# Revit family: Legrand_Electric_vehicules_charging_stations_Green_up_Metal_Connected_charging_stations
name_source: partatom
category: Equipement électrique
units: mm (PartAtom-declared; Revit-internal decimal feet)

## family parameters
Basée sur le plan de construction = Non
Configuration du panneau = Deux colonnes, circuits au sein
Cote de connecteur circulaire = Utiliser le diamètre
Couper avec des vides une fois chargée = Non
Numéro OmniClass = 23.80.30.11.17
Partagée = Non
Point de calcul de pièce = Non
Titre OmniClass = Distribution Boards and Control Panels
Toujours verticalement = Oui
Type d'élément = Tableau de raccordement

## types (20) — shared parameters
ETIM Class 6.0 = EC002883
Fabricant = Legrand
IK = 08
IP = 44
Modèle = Green'up Legrand Metal Terminal
Tension = 220
URL = www.legrand.fr
trigger safety signal transmission = 406276
zero-valued in all types: Elévation par défaut

## per-type parameters (varying)
| type | Description | General Conditions of Use | Image du type | Puissance | adjustment power | circuit breaker Protection line 2P+T (minimum) | circuit breaker diferential Protection line Type 2S | diferential | intensity Protection line 2P+T | intensity Protection line Type 2S | intensity terminal | section line 2P+T  (minimum) | section line Type 2S (minimum) | switch diferential | terminal fixing wall | terminal in place |
| Single-phase Premium Green 'up wall mount Metal - Mode 3 - 7,4kW - 32A 1 vehicle | 059004  Single-phase Premium Green 'up wall mount Metal - Mode 3 - 7,4kW - 32A 1 vehicle | https://export.legrand.com | Borne_ve_metal_murale_059011.jpg | 7.4 | 7400 W | 406884 (4500/6 kA) | 410859 (4500/6 kA) | 30 mA type F (ex Hpi) | 20 A curve C | 40 A curve C | 16 A | 3 mm  [stored 0.00984252 ft] | 10 mm  [stored 0.0328084 ft] |  | Oui | Non |
| Single-phase Premium Green 'up wall mount Metal - Mode 3  - 4,6kW - 20A 1 vehicle | 059003  Single-phase Premium Green 'up wall mount Metal - Mode 3  - 4,6kW - 20A 1 vehicle | https://export.legrand.com | Borne_ve_metal_murale_059011.jpg | 4.6 | 4600 W | 406884 (4500/6 kA) | 410755 (4500/6 kA) | 30 mA type F (ex Hpi) | 20 A curve C | 25 A curve C | 20 A | 3 mm  [stored 0.00984252 ft] | 4 mm  [stored 0.0131234 ft] |  | Oui | Non |
| Single-phase Premium Green 'up wall mount Metal - Mode 3  - 3,7kW - 16A 1 vehicle | 059003  Single-phase Premium Green 'up wall mount Metal - Mode 3  - 3,7kW - 16A 1 vehicle | https://export.legrand.com | Borne_ve_metal_murale_059011.jpg | 3.7 | 3700 W |  | 410754 (4500/6 kA) | 30 mA type F (ex Hpi) |  | 20 A curve C | 16 A | 0 mm  [stored 0 ft] | 3 mm  [stored 0.00984252 ft] |  | Oui | Non |
| Three-phase Premium Green 'up wall mount Metal - Mode 3 - 22kW - 32A 1 vehicle | 059014  Three-phase Premium Green 'up wall mount Metal - Mode 3 - 22kW - 32A 1 vehicle | https://export.legrand.com | Borne_ve_metal_murale_059011.jpg | 22 | 22000 W | 406884 (4500/6 kA) | 407902 (6000/10 kA) | 30 mA type B | 20 A curve C | 40 A curve C | 32 A | 3 mm  [stored 0.00984252 ft] | 10 mm  [stored 0.0328084 ft] | 411846 | Oui | Non |
| Single-phase Premium Green 'up wall mount Metal - Modes 2 and 3 - 3,7kW - 16A 1 vehicle | 059010  Single-phase Premium Green 'up wall mount Metal - Modes 2 and 3 - 3,7kW - 16A 1 vehicle | https://export.legrand.com | Borne_ve_metal_murale_059011.jpg | 3.7 | 3700 W |  | 410754 (4500/6 kA) | 30 mA type F (ex Hpi) |  | 20 A curve C | 20 A | 0 mm  [stored 0 ft] | 3 mm  [stored 0.00984252 ft] |  | Oui | Non |
| Single-phase Premium Green 'up wall mount Metal - Modes 2 and 3 - 4,6kW - 20A 1 vehicle | 059010  Single-phase Premium Green 'up wall mount Metal - Modes 2 and 3 - 4,6kW - 20A 1 vehicle | https://export.legrand.com | Borne_ve_metal_murale_059011.jpg | 4.6 | 4600 W | 406884 (4500/6 kA) | 410755 (4500/6 kA) | 30 mA type F (ex Hpi) | 20 A curve C | 25 A curve C | 20 A | 3 mm  [stored 0.00984252 ft] | 4 mm  [stored 0.0131234 ft] |  | Oui | Non |
| Single-phase Premium Green 'up wall mount Metal - Modes 2 and 3 - 7,4kW - 32A 1 vehicle | 059012  Single-phase Premium Green 'up wall mount Metal - Modes 2 and 3 - 7,4kW - 32A 1 vehicle | https://export.legrand.com | Borne_ve_metal_murale_059011.jpg | 7.4 | 7400 W | 406884 (4500/6 kA) | 410859 (4500/6 kA) | 30 mA type F (ex Hpi) | 20 A curve C | 40 A curve C | 32 A | 3 mm  [stored 0.00984252 ft] | 10 mm  [stored 0.0328084 ft] |  | Oui | Non |
| Single-phase Premium Green 'up Metal - Mode 3 - 3,7kW - 16A 1 vehicle | 059003 + 059054  Single-phase Premium Green 'up Metal - Mode 3 - 3,7kW - 16A 1 vehicle | https://export.legrand.com 
https://export.legrand.com | Borne_ve_metal_pied_059011_059054_pw_231663_pz_3.jpg | 3.7 | 3700 W |  | 410754 (4500/6 kA) | 30 mA type F (ex Hpi) |  | 20 A curve C | 16 A | 0 mm  [stored 0 ft] | 3 mm  [stored 0.00984252 ft] |  | Non | Oui |
| Single-phase Premium Green 'up Metal - Mode 3 - 4,6kW - 20A 1 vehicle | 059003 + 059054  Single-phase Premium Green 'up Metal - Mode 3 - 4,6kW - 20A 1 vehicle | https://export.legrand.com | Borne_ve_metal_pied_059011_059054_pw_231663_pz_3.jpg | 4.6 | 4600 W | 406884 (4500/6 kA) | 410755 (4500/6 kA) | 30 mA type F (ex Hpi) | 20 A curve C | 25 A curve C | 20 A | 3 mm  [stored 0.00984252 ft] | 4 mm  [stored 0.0131234 ft] |  | Non | Oui |
| Single-phase Premium Green 'up Metal - Mode 3 - 7,4kW - 32A 1 vehicle | 059004 + 059054 - Single-phase Premium Green 'up Metal - Mode 3 - 7,4kW - 32A 1 vehicle | https://export.legrand.com | Borne_ve_metal_murale_059011.jpg | 7.4 | 7400 W | 406884 (4500/6 kA) | 410859 (4500/6 kA) | 30 mA type F (ex Hpi) | 20 A curve C | 40 A curve C | 16 A | 3 mm  [stored 0.00984252 ft] | 10 mm  [stored 0.0328084 ft] |  | Non | Oui |
| Single-phase Premium Green 'up Metal - Modes 2 and 3 - 3,7kW - 16A 1 vehicle | 059010 + 059054  Single-phase Premium Green 'up Metal - Modes 2 and 3 - 3,7kW - 16A 1 vehicle | https://export.legrand.com | Borne_ve_metal_pied_059011_059054_pw_231663_pz_3.jpg | 3.7 | 3700 W |  | 410754 (4500/6 kA) | 30 mA type F (ex Hpi) |  | 20 A curve C | 20 A | 0 mm  [stored 0 ft] | 3 mm  [stored 0.00984252 ft] |  | Non | Oui |
| Single-phase Premium Green 'up Metal - Modes 2 and 3 - 4,6kW - 20A 1 vehicle | 059010 + 059054  Single-phase Premium Green 'up Metal - Modes 2 and 3 - 4,6kW - 20A 1 vehicle | https://export.legrand.com | Borne_ve_metal_pied_059011_059054_pw_231663_pz_3.jpg | 4.6 | 4600 W | 406884 (4500/6 kA) | 410755 (4500/6 kA) | 30 mA type F (ex Hpi) | 20 A curve C | 25 A curve C | 20 A | 3 mm  [stored 0.00984252 ft] | 4 mm  [stored 0.0131234 ft] |  | Non | Oui |
| Single-phase Premium Green 'up Metal - Modes 2 and 3 - 7,4kW - 32A 1 vehicle | 059012 + 059054  Single-phase Premium Green 'up Metal - Modes 2 and 3 - 7,4kW - 32A 1 vehicle | https://export.legrand.com | Borne_ve_metal_murale_059011.jpg | 7.4 | 7400 W | 406884 (4500/6 kA) | 410859 (4500/6 kA) | 30 mA type F (ex Hpi) | 20 A curve C | 40 A curve C | 32 A | 3 mm  [stored 0.00984252 ft] | 10 mm  [stored 0.0328084 ft] |  | Non | Oui |
| Three-phase Premium Green 'up Metal - Mode 3 - 22kW - 32A 1 vehicle | 059014 +059054   Three-phase Premium Green 'up Metal - Mode 3 - 22kW - 32A 1 vehicle | https://export.legrand.com | Borne_ve_metal_pied_059011_059054_pw_231663_pz_3.jpg | 22 | 22000 W | 406884 (4500/6 kA) | 407902 (6000/10 kA) | 30 mA type B | 20 A curve C | 40 A curve C | 32 A | 3 mm  [stored 0.00984252 ft] | 10 mm  [stored 0.0328084 ft] | 411846 | Non | Oui |
| Single-phase Premium Green 'up wall mount Metal - Modes 2 and 3 - 7,4kW - 32A 2 vehicles | 059013  Single-phase Premium Green 'up wall mount Metal - Modes 2 and 3 - 7,4kW - 32A 2 vehicles | https://export.legrand.com | Borne_ve_metal_murale_059011.jpg | 7.4 | 7400 W | 406884 (4500/6 kA) | 410859 (4500/6 kA) | 30 mA type F (ex Hpi) | 20 A curve C | 40 A curve C | 32 A | 3 mm  [stored 0.00984252 ft] | 10 mm  [stored 0.0328084 ft] |  | Oui | Non |
| Single-phase Premium Green 'up wall mount Metal - Modes 2 and 3 - 3,7kW - 16A 2 vehicles | 059011  Single-phase Premium Green 'up wall mount Metal - Modes 2 and 3 - 3,7kW - 16A 2 vehicles | https://export.legrand.com | Borne_ve_metal_murale_059011.jpg | 3.7 | 3700 W |  | 410754 (4500/6 kA) | 30 mA type F (ex Hpi) |  | 20 A curve C | 20 A | 0 mm  [stored 0 ft] | 3 mm  [stored 0.00984252 ft] |  | Oui | Non |
| Single-phase Premium Green 'up wall mount Metal - Modes 2 and 3 - 4,6kW - 20A 2 vehicles | 059011  Single-phase Premium Green 'up wall mount Metal - Modes 2 and 3 - 4,6kW - 20A 2 vehicles | https://export.legrand.com | Borne_ve_metal_murale_059011.jpg | 4.6 | 4600 W | 406884 (4500/6 kA) | 410755 (4500/6 kA) | 30 mA type F (ex Hpi) | 20 A curve C | 25 A curve C | 20 A | 3 mm  [stored 0.00984252 ft] | 4 mm  [stored 0.0131234 ft] |  | Oui | Non |
| Single-phase Premium Green 'up Metal - Modes 2 and 3 - 3,7kW - 16A 2 vehicles | 059011 + 059054  Single-phase Premium Green 'up Metal - Modes 2 and 3 - 3,7kW - 16A 2 vehicles | https://export.legrand.com | Borne_ve_metal_murale_059011.jpg | 3.7 | 3700 W |  | 410754 (4500/6 kA) | 30 mA type F (ex Hpi) |  | 20 A curve C | 20 A | 0 mm  [stored 0 ft] | 3 mm  [stored 0.00984252 ft] |  | Oui | Non |
| Single-phase Premium Green 'up Metal - Modes 2 and 3 - 4,6kW - 20A 2 vehicles | 059011 + 059054  Single-phase Premium Green 'up Metal - Modes 2 and 3 - 4,6kW - 20A 2 vehicles | https://export.legrand.com | Borne_ve_metal_murale_059011.jpg | 4.6 | 4600 W | 406884 (4500/6 kA) | 410755 (4500/6 kA) | 30 mA type F (ex Hpi) | 20 A curve C | 25 A curve C | 20 A | 3 mm  [stored 0.00984252 ft] | 4 mm  [stored 0.0131234 ft] |  | Oui | Non |
| Single-phase Premium Green 'up Metal - Modes 2 and 3 - 7,4kW - 32A 2 vehicles | 059012 + 059054  Single-phase Premium Green 'up Metal - Modes 2 and 3 - 7,4kW - 32A 2 vehicles | https://export.legrand.com | Borne_ve_metal_murale_059011.jpg | 7.4 | 7400 W | 406884 (4500/6 kA) | 410859 (4500/6 kA) | 30 mA type F (ex Hpi) | 20 A curve C | 40 A curve C | 32 A | 3 mm  [stored 0.00984252 ft] | 10 mm  [stored 0.0328084 ft] |  | Non | Oui |

note: [stored X ft] marks values corroborated as IEEE doubles in the binary element streams (Revit-internal decimal feet)
